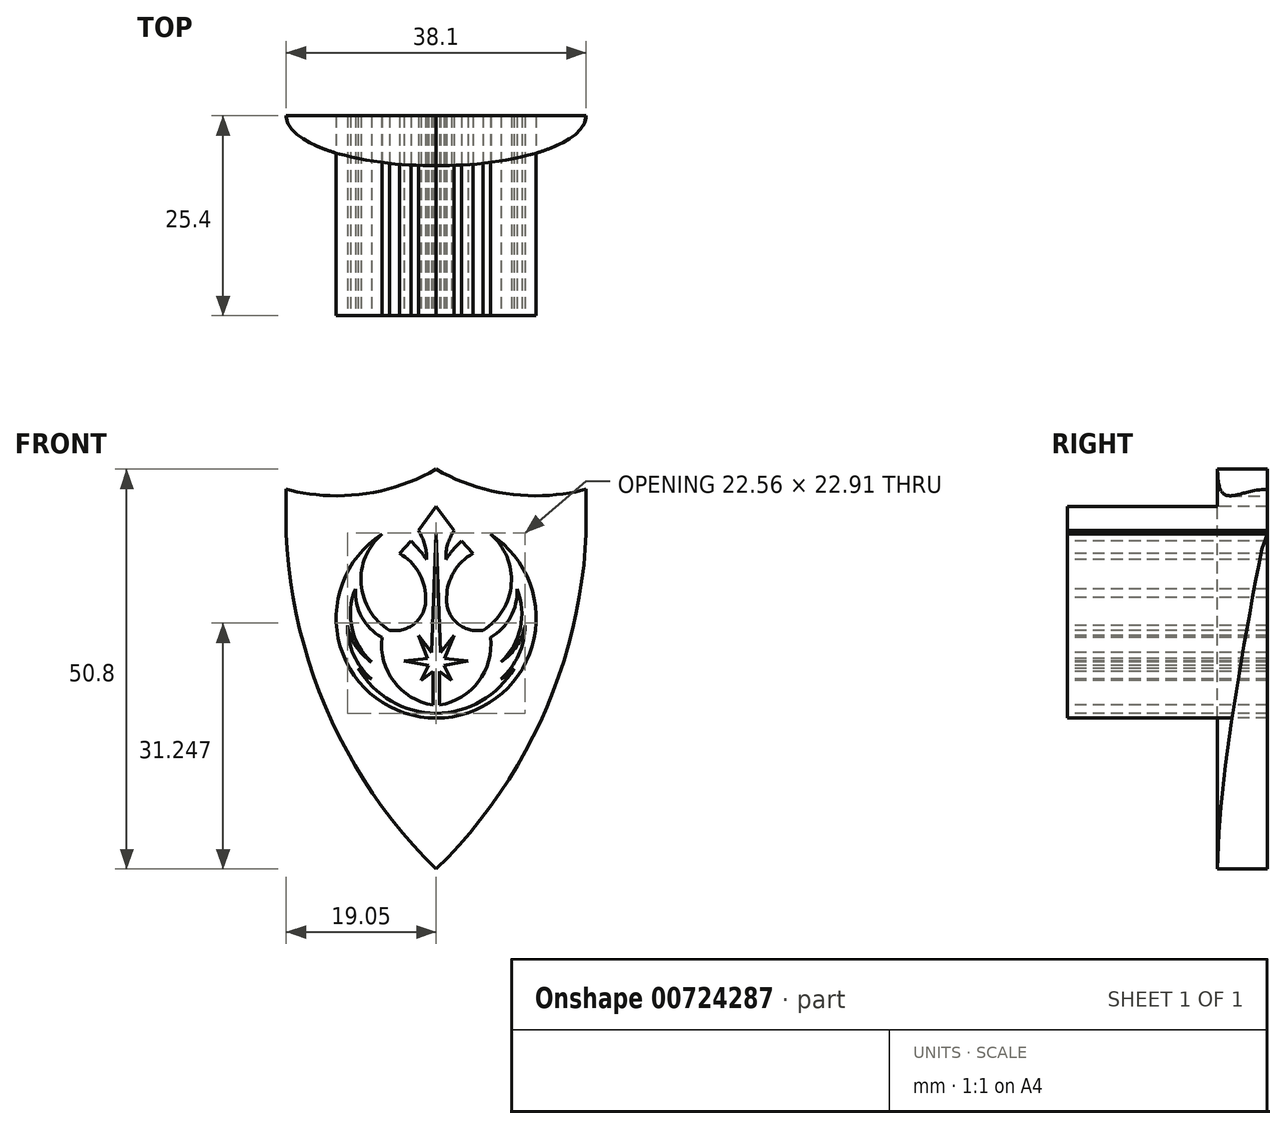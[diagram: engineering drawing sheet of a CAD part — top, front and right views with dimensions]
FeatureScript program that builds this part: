
annotation { "Feature Type Name" : "Feature", "Feature Type Description" : "" }
export const myFeature = defineFeature(function(context is Context, id is Id, definition is map)
    precondition{}
    {
        {
            var Q0;
            Q0=qCreatedBy(makeId("Front.planeOp"),FACE);
            var sketch = newSketch(context, id + "F0", { "sketchPlane" : qUnion([Q0])});
            skArc(sketch, "E0", {"start": v(-19.05, 48.26) * mm, "mid": v(-14.67, 22.1) * mm, "end": v(0, 0) * mm});
            skArc(sketch, "E1", {"start": v(-19.05, 48.26) * mm, "mid": v(-9.27, 47.65) * mm, "end": v(0, 50.8) * mm});
            skArc(sketch, "E2.MirrorCS", {"start": v(19.05, 48.26) * mm, "mid": v(9.27, 47.65) * mm, "end": v(0, 50.8) * mm});
            skArc(sketch, "E3.MirrorCS", {"start": v(19.05, 48.26) * mm, "mid": v(14.67, 22.1) * mm, "end": v(0, 0) * mm});
            skLineSegment(sketch, "E4", {"start": v(-19.05, 48.26) * mm, "end": v(-19.05, 0) * mm, "construction": true});
            skLineSegment(sketch, "E5", {"start": v(-19.05, 0) * mm, "end": v(19.05, 0) * mm});
            skSolve(sketch);
        }
        {
            var Q0;
            Q0=makeQuery(id+"F0.imprint","IMPRINT",FACE,{"disambiguationData":[TD([[makeQuery(id+"F0.imprint","IMPRINT",EDGE,{"derivedFrom":sQuery(id+"F0.wireOp",EDGE,"E0")}),1.0]])]});
            extrude(context, id + "F1", {"entities" : qUnion([Q0]), "depth" : 25.4 * mm, "offsetDistance" : 25.4 * mm});
        }
        {
            var Q0;
            Q0=makeQuery(id+"F1.opExtrude","CAP_FACE",FACE,{"disambiguationData":[OSD([sQuery(id+"F0.wireOp",EDGE,"E0"),sQuery(id+"F0.wireOp",EDGE,"E1"),sQuery(id+"F0.wireOp",EDGE,"E2.MirrorCS"),sQuery(id+"F0.wireOp",EDGE,"E3.MirrorCS")])],"isStart":false});
            var sketch = newSketch(context, id + "F2", { "sketchPlane" : qUnion([Q0])});
            skArc(sketch, "E6", {"start": v(-6.88, 42.56) * mm, "mid": v(0, 19.18) * mm, "end": v(6.88, 42.56) * mm});
            skArc(sketch, "E7", {"start": v(-10.26, 35.6) * mm, "mid": v(-9.46, 32.03) * mm, "end": v(-6.89, 29.43) * mm});
            skArc(sketch, "E8", {"start": v(-10.26, 35.6) * mm, "mid": v(-10.7, 30.64) * mm, "end": v(-8.21, 26.31) * mm});
            skArc(sketch, "E9", {"start": v(-11.28, 30.95) * mm, "mid": v(-10.21, 28.32) * mm, "end": v(-8.21, 26.31) * mm});
            skArc(sketch, "E10", {"start": v(-11.28, 30.95) * mm, "mid": v(-10.47, 27.22) * mm, "end": v(-8.21, 24.14) * mm});
            skArc(sketch, "E11", {"start": v(-9.91, 25.52) * mm, "mid": v(-9.16, 24.71) * mm, "end": v(-8.21, 24.14) * mm});
            skArc(sketch, "E12", {"start": v(-9.91, 25.52) * mm, "mid": v(-5.71, 21.35) * mm, "end": v(0, 19.8) * mm});
            skArc(sketch, "E13", {"start": v(-6.89, 29.43) * mm, "mid": v(-5.38, 23.84) * mm, "end": v(-0.42, 20.84) * mm});
            skArc(sketch, "E14", {"start": v(-1.25, 39.36) * mm, "mid": v(-1.46, 41.26) * mm, "end": v(-2.27, 42.99) * mm});
            skArc(sketch, "E15", {"start": v(-1.25, 39.36) * mm, "mid": v(-2.16, 40.57) * mm, "end": v(-3.21, 41.66) * mm});
            skArc(sketch, "E16", {"start": v(-6.88, 42.56) * mm, "mid": v(-9.54, 36.21) * mm, "end": v(-5.94, 30.35) * mm});
            skArc(sketch, "E17", {"start": v(-5.94, 30.35) * mm, "mid": v(-2.61, 31.31) * mm, "end": v(-1.33, 34.53) * mm});
            skArc(sketch, "E18", {"start": v(-1.33, 34.53) * mm, "mid": v(-2.24, 37.76) * mm, "end": v(-4.66, 40.08) * mm});
            skLineSegment(sketch, "E19", {"start": v(-4.66, 40.08) * mm, "end": v(-3.21, 41.66) * mm});
            skLineSegment(sketch, "E20", {"start": v(-2.27, 42.99) * mm, "end": v(0, 46.06) * mm});
            skLineSegment(sketch, "E21", {"start": v(-0.42, 20.84) * mm, "end": v(-0.42, 25.14) * mm});
            skLineSegment(sketch, "E22", {"start": v(-0.42, 25.14) * mm, "end": v(-1.93, 23.94) * mm});
            skLineSegment(sketch, "E23", {"start": v(-1.93, 23.94) * mm, "end": v(-0.97, 25.85) * mm});
            skLineSegment(sketch, "E24", {"start": v(-0.97, 25.85) * mm, "end": v(-4.06, 26.42) * mm});
            skLineSegment(sketch, "E25", {"start": v(-4.06, 26.42) * mm, "end": v(-1.07, 26.77) * mm});
            skLineSegment(sketch, "E26", {"start": v(-1.07, 26.77) * mm, "end": v(-2.25, 29.7) * mm});
            skLineSegment(sketch, "E27", {"start": v(-2.25, 29.7) * mm, "end": v(-0.58, 27.54) * mm});
            skLineSegment(sketch, "E28", {"start": v(-0.58, 27.54) * mm, "end": v(0, 42.7) * mm});
            skLineSegment(sketch, "E29.MirrorCS", {"start": v(2.27, 42.99) * mm, "end": v(0, 46.06) * mm});
            skArc(sketch, "E30.MirrorCS", {"start": v(1.25, 39.36) * mm, "mid": v(2.16, 40.57) * mm, "end": v(3.21, 41.66) * mm});
            skLineSegment(sketch, "E31.MirrorCS", {"start": v(4.66, 40.08) * mm, "end": v(3.21, 41.66) * mm});
            skArc(sketch, "E32.MirrorCS", {"start": v(1.33, 34.53) * mm, "mid": v(2.24, 37.76) * mm, "end": v(4.66, 40.08) * mm});
            skArc(sketch, "E33.MirrorCS", {"start": v(5.94, 30.35) * mm, "mid": v(2.61, 31.31) * mm, "end": v(1.33, 34.53) * mm});
            skArc(sketch, "E34.MirrorCS", {"start": v(6.88, 42.56) * mm, "mid": v(9.54, 36.21) * mm, "end": v(5.94, 30.35) * mm});
            skArc(sketch, "E35.MirrorCS", {"start": v(10.26, 35.6) * mm, "mid": v(9.46, 32.03) * mm, "end": v(6.89, 29.43) * mm});
            skArc(sketch, "E36.MirrorCS", {"start": v(10.26, 35.6) * mm, "mid": v(10.7, 30.64) * mm, "end": v(8.21, 26.31) * mm});
            skArc(sketch, "E37.MirrorCS", {"start": v(11.28, 30.95) * mm, "mid": v(10.21, 28.32) * mm, "end": v(8.21, 26.31) * mm});
            skArc(sketch, "E38.MirrorCS", {"start": v(11.28, 30.95) * mm, "mid": v(10.47, 27.22) * mm, "end": v(8.21, 24.14) * mm});
            skArc(sketch, "E39.MirrorCS", {"start": v(9.91, 25.52) * mm, "mid": v(9.16, 24.71) * mm, "end": v(8.21, 24.14) * mm});
            skArc(sketch, "E40.MirrorCS", {"start": v(9.91, 25.52) * mm, "mid": v(5.71, 21.35) * mm, "end": v(0, 19.8) * mm});
            skLineSegment(sketch, "E41.MirrorCS", {"start": v(0.42, 20.84) * mm, "end": v(0.42, 25.14) * mm});
            skLineSegment(sketch, "E42.MirrorCS", {"start": v(0.42, 25.14) * mm, "end": v(1.93, 23.94) * mm});
            skLineSegment(sketch, "E43.MirrorCS", {"start": v(1.93, 23.94) * mm, "end": v(0.97, 25.85) * mm});
            skLineSegment(sketch, "E44.MirrorCS", {"start": v(0.97, 25.85) * mm, "end": v(4.06, 26.42) * mm});
            skLineSegment(sketch, "E45.MirrorCS", {"start": v(4.06, 26.42) * mm, "end": v(1.07, 26.77) * mm});
            skLineSegment(sketch, "E46.MirrorCS", {"start": v(1.07, 26.77) * mm, "end": v(2.25, 29.7) * mm});
            skLineSegment(sketch, "E47.MirrorCS", {"start": v(2.25, 29.7) * mm, "end": v(0.58, 27.54) * mm});
            skLineSegment(sketch, "E48.MirrorCS", {"start": v(0.58, 27.54) * mm, "end": v(0, 42.7) * mm});
            skArc(sketch, "E49.MirrorCS", {"start": v(1.25, 39.36) * mm, "mid": v(1.46, 41.26) * mm, "end": v(2.27, 42.99) * mm});
            skArc(sketch, "E50.MirrorCS", {"start": v(6.89, 29.43) * mm, "mid": v(5.38, 23.84) * mm, "end": v(0.42, 20.84) * mm});
            skSolve(sketch);
        }
        {
            var Q0;
            Q0=makeQuery(id+"F2.imprint","IMPRINT",FACE,{"disambiguationData":[TD([[makeQuery(id+"F2.imprint","IMPRINT",EDGE,{"derivedFrom":sQuery(id+"F2.wireOp",EDGE,"E7")}),-1.0]])]});
            extrude(context, id + "F3", {"entities" : qUnion([Q0]), "operationType" : NewBodyOperationType.ADD, "depth" : 2.54 * mm, "offsetDistance" : 25.4 * mm});
        }
        {
            var Q0;
            Q0=makeQuery(id+"F2.imprint","IMPRINT",FACE,{"disambiguationData":[TD([[makeQuery(id+"F2.imprint","IMPRINT",EDGE,{"derivedFrom":sQuery(id+"F2.wireOp",EDGE,"E6")}),1.0]])]});
            extrude(context, id + "F4", {"entities" : qUnion([Q0]), "operationType" : NewBodyOperationType.ADD, "depth" : 1.27 * mm, "offsetDistance" : 25.4 * mm});
        }
        {
            var Q0;
            Q0=sQuery(id+"F0.wireOp",EDGE,"E5");
            extrude(context, id + "F5", {"bodyType" : ToolBodyType.SURFACE, "surfaceEntities" : qUnion([Q0]), "depth" : 25.4 * mm, "offsetDistance" : 25.4 * mm});
        }
        {
            var Q0;
            Q0=makeQuery(id+"F5.opExtrude","SWEPT_FACE",FACE,{"disambiguationData":[OSD([sQuery(id+"F0.wireOp",EDGE,"E5")])]});
            var sketch = newSketch(context, id + "F6", { "sketchPlane" : qUnion([Q0])});
            skEllipticalArc(sketch, "E51", {});
            skLineSegment(sketch, "E52.0", {"start": v(-19.05, 0) * mm, "end": v(19.05, 0) * mm});
            skFitSpline(sketch, "E53.0", {"points": [v(-19.6, 0.81) * mm, v(-19.73, 0) * mm, v(-19.6, -0.81) * mm, v(-19.26, -1.58) * mm, v(-18.73, -2.28) * mm, v(-18.03, -2.93) * mm, v(-17.16, -3.54) * mm, v(-15.8, -4.3) * mm, v(-13.75, -5.12) * mm, v(-11.3, -5.8) * mm, v(-9.1, -6.24) * mm, v(-6.8, -6.6) * mm, v(-4.4, -6.84) * mm, v(-1.9, -6.96) * mm, v(0, -7) * mm, v(1.9, -6.96) * mm, v(4.4, -6.84) * mm, v(6.8, -6.6) * mm, v(9.1, -6.24) * mm, v(11.3, -5.8) * mm, v(13.75, -5.12) * mm, v(15.8, -4.3) * mm, v(17.16, -3.54) * mm, v(18.03, -2.93) * mm, v(18.73, -2.28) * mm, v(19.26, -1.58) * mm, v(19.6, -0.81) * mm, v(19.73, 0) * mm, v(19.6, 0.81) * mm, v(19.26, 1.58) * mm, v(18.73, 2.28) * mm, v(18.03, 2.93) * mm, v(17.16, 3.54) * mm, v(15.8, 4.3) * mm, v(13.75, 5.12) * mm, v(11.3, 5.8) * mm, v(9.1, 6.24) * mm, v(6.8, 6.6) * mm, v(4.4, 6.84) * mm, v(1.9, 6.96) * mm, v(0, 7) * mm, v(-1.9, 6.96) * mm, v(-4.4, 6.84) * mm, v(-6.8, 6.6) * mm, v(-9.1, 6.24) * mm, v(-11.3, 5.8) * mm, v(-13.75, 5.12) * mm, v(-15.8, 4.3) * mm, v(-17.16, 3.54) * mm, v(-18.03, 2.93) * mm, v(-18.73, 2.28) * mm, v(-19.26, 1.58) * mm, v(-19.6, 0.81) * mm, v(-19.73, 0) * mm, v(-19.6, -0.81) * mm]});
            skFitSpline(sketch, "E54.0", {"points": [v(-20.22, 1) * mm, v(-20.37, 0) * mm, v(-20.22, -1) * mm, v(-19.8, -1.9) * mm, v(-19.2, -2.71) * mm, v(-18.42, -3.43) * mm, v(-17.5, -4.08) * mm, v(-16.07, -4.87) * mm, v(-13.95, -5.73) * mm, v(-11.44, -6.42) * mm, v(-9.21, -6.86) * mm, v(-6.89, -7.23) * mm, v(-4.44, -7.47) * mm, v(-1.92, -7.6) * mm, v(0, -7.63) * mm, v(1.92, -7.6) * mm, v(4.44, -7.47) * mm, v(6.89, -7.23) * mm, v(9.21, -6.86) * mm, v(11.44, -6.42) * mm, v(13.95, -5.73) * mm, v(16.07, -4.87) * mm, v(17.5, -4.08) * mm, v(18.42, -3.43) * mm, v(19.2, -2.71) * mm, v(19.8, -1.9) * mm, v(20.22, -1) * mm, v(20.37, 0) * mm, v(20.22, 1) * mm, v(19.8, 1.9) * mm, v(19.2, 2.71) * mm, v(18.42, 3.43) * mm, v(17.5, 4.08) * mm, v(16.07, 4.87) * mm, v(13.95, 5.73) * mm, v(11.44, 6.42) * mm, v(9.21, 6.86) * mm, v(6.89, 7.23) * mm, v(4.44, 7.47) * mm, v(1.92, 7.6) * mm, v(0, 7.63) * mm, v(-1.92, 7.6) * mm, v(-4.44, 7.47) * mm, v(-6.89, 7.23) * mm, v(-9.21, 6.86) * mm, v(-11.44, 6.42) * mm, v(-13.95, 5.73) * mm, v(-16.07, 4.87) * mm, v(-17.5, 4.08) * mm, v(-18.42, 3.43) * mm, v(-19.2, 2.71) * mm, v(-19.8, 1.9) * mm, v(-20.22, 1) * mm, v(-20.37, 0) * mm, v(-20.22, -1) * mm]});
            const initialGuessF6  = {"E51": [0, 0, -1, 0, 0.01905, 0.00635, 3.141592653589793, 0]};
            skSetInitialGuess(sketch, initialGuessF6);
            skSolve(sketch);
        }
        {
            var Q0;
            Q0=makeQuery(id+"F6.imprint","IMPRINT",FACE,{"disambiguationData":[TD([[makeQuery(id+"F6.imprint","IMPRINT",EDGE,{"derivedFrom":sQuery(id+"F6.wireOp",EDGE,"E51")}),1.0]])]});
            extrude(context, id + "F7", {"entities" : qUnion([Q0]), "operationType" : NewBodyOperationType.INTERSECT, "endBound" : BoundingType.THROUGH_ALL, "oppositeDirection" : true, "depth" : 25.4 * mm, "offsetDistance" : 25.4 * mm});
        }
        {
            var Q0;
            Q0 = qSketchRegion(id + "F2", true);
            extrude(context, id + "F8", {"entities" : qUnion([Q0]), "oppositeDirection" : true, "depth" : 25.4 * mm, "offsetDistance" : 25.4 * mm});
        }
        {
            var Q0;
            {var subQ0=sQuery(id+"F6.wireOp",EDGE,"E51");Q0=makeQuery(id+"F6.imprint","IMPRINT",FACE,{"disambiguationData":[TD([[makeQuery(id+"F6.imprint","IMPRINT",EDGE,{"derivedFrom":subQ0}),-1.0]])]});}
            var Q1;
            Q1=makeQuery(id+"F6.imprint","IMPRINT",FACE,{"disambiguationData":[TD([[makeQuery(id+"F6.imprint","IMPRINT",EDGE,{"derivedFrom":sQuery(id+"F6.wireOp",EDGE,"E51")}),1.0]])]});
            extrude(context, id + "F9", {"entities" : qUnion([Q0, Q1]), "operationType" : NewBodyOperationType.INTERSECT, "endBound" : BoundingType.THROUGH_ALL, "oppositeDirection" : true, "depth" : 25.4 * mm, "offsetDistance" : 25.4 * mm});
        }
        {
            var Q0;
            Q0=makeQuery(id+"F2.imprint","IMPRINT",FACE,{"disambiguationData":[TD([[makeQuery(id+"F2.imprint","IMPRINT",EDGE,{"derivedFrom":sQuery(id+"F2.wireOp",EDGE,"E7")}),-1.0]])]});
            extrude(context, id + "F10", {"entities" : qUnion([Q0]), "oppositeDirection" : true, "depth" : 25.4 * mm, "offsetDistance" : 25.4 * mm});
        }
        {
            var Q0;
            {var subQ0=sQuery(id+"F6.wireOp",EDGE,"E53.0");var subQ1=makeQuery(id+"F5.opExtrude","SWEPT_EDGE",EDGE,{"disambiguationData":[OSD([sQuery(id+"F0.wireOp",VERTEX,"E5.start")])]});var subQ2=makeQuery(id+"F6.imprint","INTERSECT",VERTEX,{"derivedFrom":[subQ1,subQ0]});Q0=makeQuery(id+"F6.imprint","IMPRINT",FACE,{"disambiguationData":[TD([[makeQuery(id+"F6.imprint","IMPRINT",EDGE,{"disambiguationData":[TD([[subQ2,1.0]])],"derivedFrom":subQ0}),-1.0]])]});}
            var Q1;
            {var subQ0=sQuery(id+"F6.wireOp",EDGE,"E51");Q1=makeQuery(id+"F6.imprint","IMPRINT",FACE,{"disambiguationData":[TD([[makeQuery(id+"F6.imprint","IMPRINT",EDGE,{"derivedFrom":subQ0}),-1.0]])]});}
            var Q2;
            Q2=makeQuery(id+"F6.imprint","IMPRINT",FACE,{"disambiguationData":[TD([[makeQuery(id+"F6.imprint","IMPRINT",EDGE,{"derivedFrom":sQuery(id+"F6.wireOp",EDGE,"E51")}),1.0]])]});
            extrude(context, id + "F11", {"entities" : qUnion([Q0, Q1, Q2]), "operationType" : NewBodyOperationType.INTERSECT, "endBound" : BoundingType.THROUGH_ALL, "oppositeDirection" : true, "depth" : 25.4 * mm, "offsetDistance" : 25.4 * mm});
        }
        {
            var Q0;
            Q0=makeQuery(id+"F5.opExtrude","SWEPT_BODY",BODY,{"disambiguationData":[OSD([sQuery(id+"F0.wireOp",EDGE,"E5")])]});
            deleteBodies(context, id + "F12", {"entities" : qUnion([Q0])});
        }
    });
